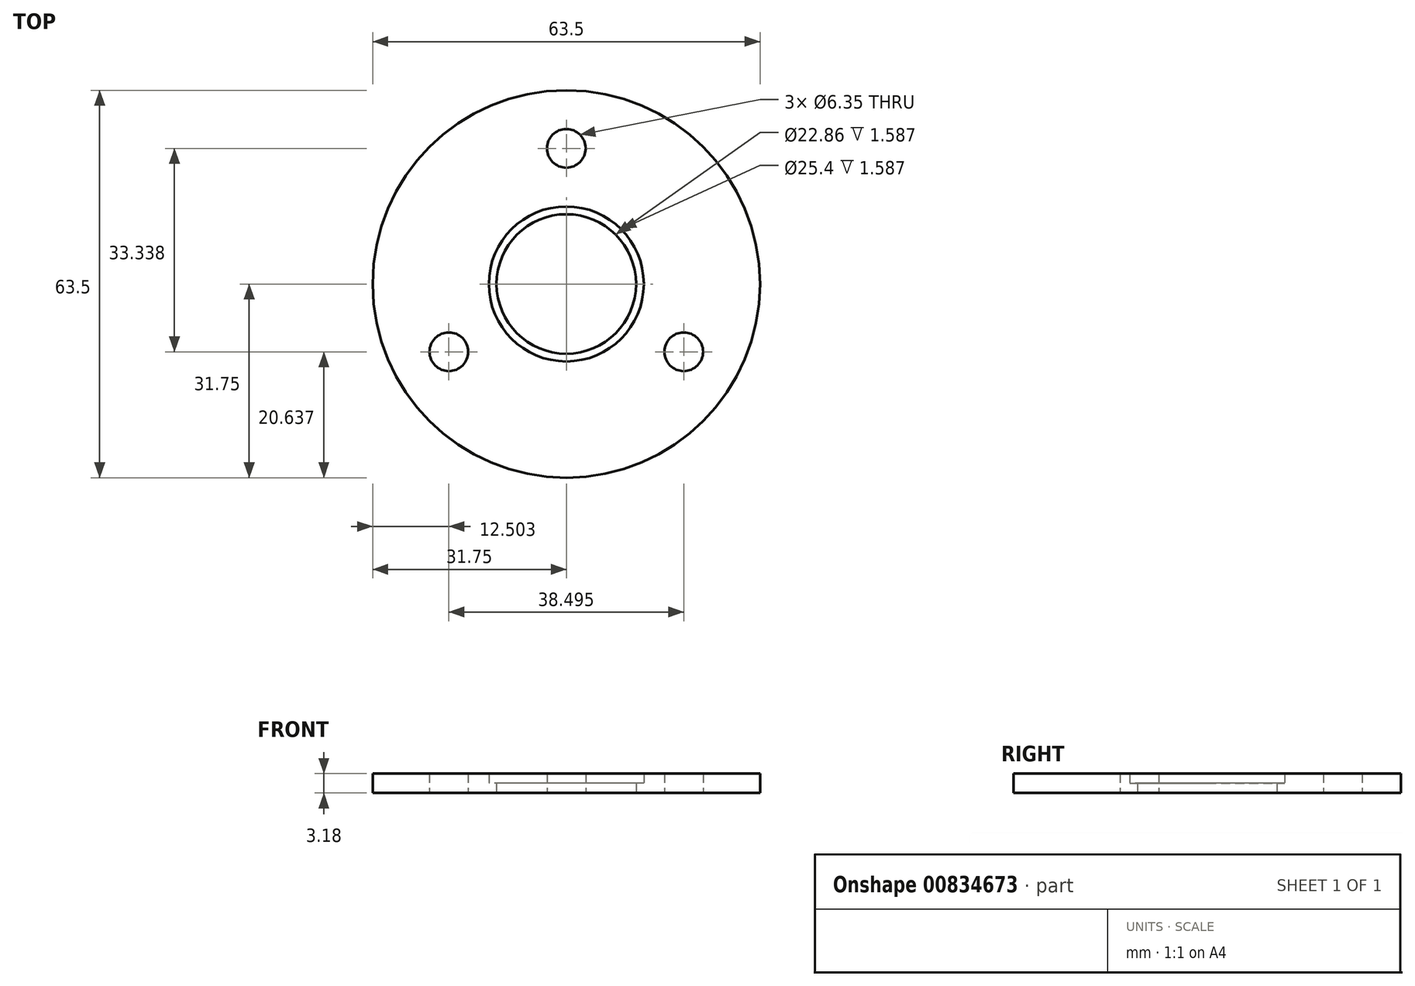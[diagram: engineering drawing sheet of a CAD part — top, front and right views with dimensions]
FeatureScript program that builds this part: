
annotation { "Feature Type Name" : "Feature", "Feature Type Description" : "" }
export const myFeature = defineFeature(function(context is Context, id is Id, definition is map)
    precondition{}
    {
        {
            var Q0;
            Q0=qCreatedBy(makeId("Top.planeOp"),FACE);
            var sketch = newSketch(context, id + "F0", { "sketchPlane" : qUnion([Q0])});
            skCircle(sketch, "E0", {"center": v(0, 0) * mm, "radius": 31.75 * mm});
            skCircle(sketch, "E1", {"center": v(0, 0) * mm, "radius": 11.43 * mm});
            skCircle(sketch, "E2.cCircle", {"center": v(0, 0) * mm, "radius": 31.75 * mm, "construction": true});
            skLineSegment(sketch, "E2.0", {"start": v(27.5, -15.87) * mm, "end": v(-27.5, -15.87) * mm, "construction": true});
            skLineSegment(sketch, "E2.1", {"start": v(-27.5, -15.88) * mm, "end": v(0, 31.75) * mm, "construction": true});
            skLineSegment(sketch, "E2.2", {"start": v(0, 31.75) * mm, "end": v(27.5, -15.88) * mm, "construction": true});
            skLineSegment(sketch, "E3", {"start": v(0, 31.75) * mm, "end": v(0, 0) * mm, "construction": true});
            skLineSegment(sketch, "E4", {"start": v(-27.5, -15.88) * mm, "end": v(0, 0) * mm, "construction": true});
            skLineSegment(sketch, "E5", {"start": v(27.5, -15.87) * mm, "end": v(0, 0) * mm, "construction": true});
            skCircle(sketch, "E6", {"center": v(0, 0) * mm, "radius": 22.23 * mm, "construction": true});
            skCircle(sketch, "E7", {"center": v(19.25, -11.11) * mm, "radius": 3.18 * mm});
            skCircle(sketch, "E8", {"center": v(-19.25, -11.11) * mm, "radius": 3.18 * mm});
            skCircle(sketch, "E9", {"center": v(0, 22.23) * mm, "radius": 3.18 * mm});
            skLineSegment(sketch, "E10", {"start": v(0, 0) * mm, "end": v(0, -15.88) * mm, "construction": true});
            skCircle(sketch, "E11", {"center": v(0, 0) * mm, "radius": 12.7 * mm});
            skSolve(sketch);
        }
        {
            var Q0;
            Q0=makeQuery(id+"F0.imprint","IMPRINT",FACE,{"disambiguationData":[TD([[makeQuery(id+"F0.imprint","IMPRINT",EDGE,{"derivedFrom":sQuery(id+"F0.wireOp",EDGE,"E1")}),-1.0]])]});
            extrude(context, id + "F1", {"entities" : qUnion([Q0]), "depth" : 1.59 * mm, "offsetDistance" : 25.4 * mm});
        }
        {
            var Q0;
            Q0=makeQuery(id+"F0.imprint","IMPRINT",FACE,{"disambiguationData":[TD([[makeQuery(id+"F0.imprint","IMPRINT",EDGE,{"derivedFrom":sQuery(id+"F0.wireOp",EDGE,"E0")}),1.0]])]});
            extrude(context, id + "F2", {"entities" : qUnion([Q0]), "operationType" : NewBodyOperationType.ADD, "depth" : 3.17 * mm, "offsetDistance" : 25.4 * mm});
        }
    });
